# Revit family: BIM_KUBAIR F400 CC INTZ Horizontal
name_source: partatom
category: Equipement de génie climatique
revit_build: Autodesk Revit 2016 (Build: 20161004_0715(x64)
units: mm (PartAtom-declared; Revit-internal decimal feet)

## family parameters
Basée sur le plan de construction = Non
Cote de connecteur circulaire = Utiliser le diamètre
Couper avec des vides une fois chargée = Non
Numéro OmniClass = 23.75.00.00
Partagée = Non
Point de calcul de pièce = Oui
Titre OmniClass = Climate Control (HVAC)
Toujours verticalement = Oui
Type d'élément = Normal

## types (75) — shared parameters
Classe_de_protection_electrique = F
Consignes – raccordements aérauliques = Raccorder 1, 2 ou 3 ouies  au refoulement et 1, 2 ou 3 ouies à l’aspiration
Fabricant = VIM
Hauteur_equerre = 200 mm  [stored 0.656168 ft]
Hauteur_support = 30 mm  [stored 0.0984252 ft]
IfcExportAs = IfcFan
IfcExportType = IfcFlowMovingDevice
Largeur_equerre = 218 mm  [stored 0.715223 ft]
Lien_page_produit = http://www.vim.fr
Materiau_caisson = Acier, galvanisé
Materiau_support = Acier
Protection_IP = IP 55
Visibilité_marque = Oui

## per-type parameters (varying)
| type | A | BH | C | Code_article | Courant_nominal | D | Debit_maxi | Debit_mini | EC | F | J | KC | Modèle | Nombre_de_phases | Poids | Position_A_equerre | Prof_INTZ | Puissance_electrique | Tension_nominale |
| KUBAIR F400 CC 355 4PM INTZ 0,25kW Horizontal | 627 mm  [stored 2.05709 ft] | 695 mm  [stored 2.28018 ft] | 263 mm  [stored 0.862861 ft] | 644533 + 660100 | 3 A | 559 mm  [stored 1.83399 ft] | 3090 m³/h | 900 m³/h | 790 mm  [stored 2.59186 ft] | 660 mm  [stored 2.16535 ft] | 102 mm | 954 mm  [stored 3.12992 ft] | KUBAIR F400 CC 355 4PM INTZ 0,25kW Caisson Horizontal | 1 | 59 Kg | 155 mm  [stored 0.50853 ft] | 100 mm  [stored 0.328084 ft] | 250 W | 230 V |
| KUBAIR F400 CC 355 6PM INTZ 0,18kW Horizontal | 627 mm  [stored 2.05709 ft] | 695 mm  [stored 2.28018 ft] | 263 mm  [stored 0.862861 ft] | 644537 + 660100 | 2 A | 559 mm  [stored 1.83399 ft] | 2140 m³/h | 620 m³/h | 790 mm  [stored 2.59186 ft] | 660 mm  [stored 2.16535 ft] | 102 mm | 954 mm  [stored 3.12992 ft] | KUBAIR F400 CC 355 6PM INTZ 0,18kW Caisson Horizontal | 1 | 59 Kg | 155 mm  [stored 0.50853 ft] | 100 mm  [stored 0.328084 ft] | 180 W | 230 V |
| KUBAIR F400 CC 355 4PT IE1 INTZ 0,25kW Horizontal | 627 mm  [stored 2.05709 ft] | 695 mm  [stored 2.28018 ft] | 263 mm  [stored 0.862861 ft] | 644541 + 660100 | 1 A | 559 mm  [stored 1.83399 ft] | 3090 m³/h | 900 m³/h | 790 mm  [stored 2.59186 ft] | 660 mm  [stored 2.16535 ft] | 102 mm | 954 mm  [stored 3.12992 ft] | KUBAIR F400 CC 355 4PT IE1 INTZ 0,25kW Caisson Horizontal | 3 | 59 Kg | 155 mm  [stored 0.50853 ft] | 100 mm  [stored 0.328084 ft] | 250 W | 400 V |
| KUBAIR F400 CC 355 4PT IE2 INTZ 0,25kW Horizontal | 627 mm  [stored 2.05709 ft] | 695 mm  [stored 2.28018 ft] | 263 mm  [stored 0.862861 ft] | 644545 + 660100 | 1 A | 559 mm  [stored 1.83399 ft] | 3090 m³/h | 900 m³/h | 790 mm  [stored 2.59186 ft] | 660 mm  [stored 2.16535 ft] | 102 mm | 954 mm  [stored 3.12992 ft] | KUBAIR F400 CC 355 4PT IE2 INTZ 0,25kW Caisson Horizontal | 3 | 59 Kg | 155 mm  [stored 0.50853 ft] | 100 mm  [stored 0.328084 ft] | 250 W | 400 V |
| KUBAIR F400 CC 355 4PT IE3 INTZ 0,25kW Horizontal | 627 mm  [stored 2.05709 ft] | 695 mm  [stored 2.28018 ft] | 263 mm  [stored 0.862861 ft] | 644549 + 660100 | 1 A | 559 mm  [stored 1.83399 ft] | 3090 m³/h | 900 m³/h | 790 mm  [stored 2.59186 ft] | 660 mm  [stored 2.16535 ft] | 102 mm | 954 mm  [stored 3.12992 ft] | KUBAIR F400 CC 355 4PT IE3 INTZ 0,25kW Caisson Horizontal | 3 | 59 Kg | 155 mm  [stored 0.50853 ft] | 100 mm  [stored 0.328084 ft] | 250 W | 400 V |
| KUBAIR F400 CC 355 6PT IE1 INTZ 0,18kW Horizontal | 627 mm  [stored 2.05709 ft] | 695 mm  [stored 2.28018 ft] | 263 mm  [stored 0.862861 ft] | 644553 + 660100 | 1 A | 559 mm  [stored 1.83399 ft] | 2140 m³/h | 620 m³/h | 790 mm  [stored 2.59186 ft] | 660 mm  [stored 2.16535 ft] | 102 mm | 954 mm  [stored 3.12992 ft] | KUBAIR F400 CC 355 6PT IE1 INTZ 0,18kW Caisson Horizontal | 3 | 59 Kg | 155 mm  [stored 0.50853 ft] | 100 mm  [stored 0.328084 ft] | 180 W | 400 V |
| KUBAIR F400 CC 355 6PT IE2 INTZ 0,18kW Horizontal | 627 mm  [stored 2.05709 ft] | 695 mm  [stored 2.28018 ft] | 263 mm  [stored 0.862861 ft] | 644557 + 660100 | 1 A | 559 mm  [stored 1.83399 ft] | 2140 m³/h | 620 m³/h | 790 mm  [stored 2.59186 ft] | 660 mm  [stored 2.16535 ft] | 102 mm | 954 mm  [stored 3.12992 ft] | KUBAIR F400 CC 355 6PT IE2 INTZ 0,18kW Caisson Horizontal | 3 | 59 Kg | 155 mm  [stored 0.50853 ft] | 100 mm  [stored 0.328084 ft] | 180 W | 400 V |
| KUBAIR F400 CC 355 6PT IE3 INTZ 0,18kW Horizontal | 627 mm  [stored 2.05709 ft] | 695 mm  [stored 2.28018 ft] | 263 mm  [stored 0.862861 ft] | 644561 + 660100 | 1 A | 559 mm  [stored 1.83399 ft] | 2140 m³/h | 620 m³/h | 790 mm  [stored 2.59186 ft] | 660 mm  [stored 2.16535 ft] | 102 mm | 954 mm  [stored 3.12992 ft] | KUBAIR F400 CC 355 6PT IE3 INTZ 0,18kW Caisson Horizontal | 3 | 59 Kg | 155 mm  [stored 0.50853 ft] | 100 mm  [stored 0.328084 ft] | 180 W | 400 V |
| KUBAIR F400 CC 355 4/6PT INTZ 0,30/0,10kW Horizontal | 627 mm  [stored 2.05709 ft] | 695 mm  [stored 2.28018 ft] | 263 mm  [stored 0.862861 ft] | 644565 + 660100 | 1 A | 559 mm  [stored 1.83399 ft] | 3090 m³/h | 900 m³/h | 790 mm  [stored 2.59186 ft] | 660 mm  [stored 2.16535 ft] | 102 mm | 954 mm  [stored 3.12992 ft] | KUBAIR F400 CC 355 4/6PT INTZ 0,30/0,10kW Caisson Horizontal | 3 | 61 Kg | 155 mm  [stored 0.50853 ft] | 100 mm  [stored 0.328084 ft] | 300 W | 400 V |
| KUBAIR F400 CC 355 4/8PT INTZ 0,60/0,15kW Horizontal | 627 mm  [stored 2.05709 ft] | 695 mm  [stored 2.28018 ft] | 263 mm  [stored 0.862861 ft] | 644569 + 660100 | 2 A | 559 mm  [stored 1.83399 ft] | 3090 m³/h | 900 m³/h | 790 mm  [stored 2.59186 ft] | 660 mm  [stored 2.16535 ft] | 102 mm | 954 mm  [stored 3.12992 ft] | KUBAIR F400 CC 355 4/8PT INTZ 0,60/0,15kW Caisson Horizontal | 3 | 61 Kg | 155 mm  [stored 0.50853 ft] | 100 mm  [stored 0.328084 ft] | 600 W | 400 V |
| KUBAIR F400 CC 400 4PM INTZ 0,55kW Horizontal | 699 mm  [stored 2.29331 ft] | 767 mm  [stored 2.5164 ft] | 297 mm  [stored 0.974409 ft] | 644573 + 660101 | 4 A | 631 mm  [stored 2.07021 ft] | 5000 m³/h | 1060 m³/h | 864 mm  [stored 2.83465 ft] | 732 mm | 102 mm | 1022 mm | KUBAIR F400 CC 400 4PM INTZ 0,55kW Caisson Horizontal | 1 | 72 Kg | 155 mm  [stored 0.50853 ft] | 120 mm  [stored 0.393701 ft] | 550 W | 230 V |
| KUBAIR F400 CC 400 6PM INTZ 0,25kW Horizontal | 699 mm  [stored 2.29331 ft] | 767 mm  [stored 2.5164 ft] | 297 mm  [stored 0.974409 ft] | 644577 + 660101
644577 + 660101 | 2 A | 631 mm  [stored 2.07021 ft] | 3310 m³/h | 520 m³/h | 864 mm  [stored 2.83465 ft] | 732 mm | 102 mm | 1022 mm | KUBAIR F400 CC 400 6PM INTZ 0,25kW Caisson Horizontal | 1 | 72 Kg | 155 mm  [stored 0.50853 ft] | 120 mm  [stored 0.393701 ft] | 250 W | 230 V |
| KUBAIR F400 CC 400 4PT IE1 INTZ 0,55kW Horizontal | 699 mm  [stored 2.29331 ft] | 767 mm  [stored 2.5164 ft] | 297 mm  [stored 0.974409 ft] | 644581 + 660101 | 1 A | 631 mm  [stored 2.07021 ft] | 5000 m³/h | 1060 m³/h | 864 mm  [stored 2.83465 ft] | 732 mm | 102 mm | 1022 mm | KUBAIR F400 CC 400 4PT IE1 INTZ 0,55kW Caisson Horizontal | 3 | 72 Kg | 155 mm  [stored 0.50853 ft] | 120 mm  [stored 0.393701 ft] | 550 W | 400 V |
| KUBAIR F400 CC 400 4PT IE2 INTZ 0,55kW Horizontal | 699 mm  [stored 2.29331 ft] | 767 mm  [stored 2.5164 ft] | 297 mm  [stored 0.974409 ft] | 644585 + 660101 | 1 A | 631 mm  [stored 2.07021 ft] | 5000 m³/h | 1060 m³/h | 864 mm  [stored 2.83465 ft] | 732 mm | 102 mm | 1022 mm | KUBAIR F400 CC 400 4PT IE2 INTZ 0,55kW Caisson Horizontal | 3 | 72 Kg | 155 mm  [stored 0.50853 ft] | 120 mm  [stored 0.393701 ft] | 550 W | 400 V |
| KUBAIR F400 CC 400 4PT IE3 INTZ 0,55kW Horizontal | 699 mm  [stored 2.29331 ft] | 767 mm  [stored 2.5164 ft] | 297 mm  [stored 0.974409 ft] | 644589 + 660101 | 1 A | 631 mm  [stored 2.07021 ft] | 5000 m³/h | 1060 m³/h | 864 mm  [stored 2.83465 ft] | 732 mm | 102 mm | 1022 mm | KUBAIR F400 CC 400 4PT IE3 INTZ 0,55kW Caisson Horizontal | 3 | 72 Kg | 155 mm  [stored 0.50853 ft] | 120 mm  [stored 0.393701 ft] | 550 W | 400 V |
| KUBAIR F400 CC 400 6PT IE1 INTZ 0,37kW Horizontal | 699 mm  [stored 2.29331 ft] | 767 mm  [stored 2.5164 ft] | 297 mm  [stored 0.974409 ft] | 644593 + 660101 | 1 A | 631 mm  [stored 2.07021 ft] | 3310 m³/h | 520 m³/h | 864 mm  [stored 2.83465 ft] | 732 mm | 102 mm | 1022 mm | KUBAIR F400 CC 400 6PT IE1 INTZ 0,37kW Caisson Horizontal | 3 | 72 Kg | 155 mm  [stored 0.50853 ft] | 120 mm  [stored 0.393701 ft] | 370 W | 400 V |
| KUBAIR F400 CC 400 6PT IE2 INTZ 0,37kW Horizontal | 699 mm  [stored 2.29331 ft] | 767 mm  [stored 2.5164 ft] | 297 mm  [stored 0.974409 ft] | 644597 + 660101 | 1 A | 631 mm  [stored 2.07021 ft] | 3310 m³/h | 520 m³/h | 864 mm  [stored 2.83465 ft] | 732 mm | 102 mm | 1022 mm | KUBAIR F400 CC 400 6PT IE2 INTZ 0,37kW Caisson Horizontal | 3 | 72 Kg | 155 mm  [stored 0.50853 ft] | 120 mm  [stored 0.393701 ft] | 370 W | 400 V |
| KUBAIR F400 CC 400 6PT IE3 INTZ 0,37kW Horizontal | 699 mm  [stored 2.29331 ft] | 767 mm  [stored 2.5164 ft] | 297 mm  [stored 0.974409 ft] | 644601 + 660101 | 1 A | 631 mm  [stored 2.07021 ft] | 3310 m³/h | 520 m³/h | 864 mm  [stored 2.83465 ft] | 732 mm | 102 mm | 1022 mm | KUBAIR F400 CC 400 6PT IE3 INTZ 0,37kW Caisson Horizontal | 3 | 72 Kg | 155 mm  [stored 0.50853 ft] | 120 mm  [stored 0.393701 ft] | 370 W | 400 V |
| KUBAIR F400 CC 400 4/6PT INTZ 0,55/0,20kW Horizontal | 699 mm  [stored 2.29331 ft] | 767 mm  [stored 2.5164 ft] | 297 mm  [stored 0.974409 ft] | 644605 + 660101 | 2 A | 631 mm  [stored 2.07021 ft] | 5000 m³/h | 1060 m³/h | 864 mm  [stored 2.83465 ft] | 732 mm | 102 mm | 1022 mm | KUBAIR F400 CC 400 4/6PT INTZ 0,55/0,20kW Caisson Horizontal | 3 | 74 Kg | 155 mm  [stored 0.50853 ft] | 120 mm  [stored 0.393701 ft] | 550 W | 400 V |
| KUBAIR F400 CC 400 4/8PT INTZ 0,60/0,15kW Horizontal | 699 mm  [stored 2.29331 ft] | 767 mm  [stored 2.5164 ft] | 297 mm  [stored 0.974409 ft] | 644609 + 660101 | 2 A | 631 mm  [stored 2.07021 ft] | 5000 m³/h | 1060 m³/h | 864 mm  [stored 2.83465 ft] | 732 mm | 102 mm | 1022 mm | KUBAIR F400 CC 400 4/8PT INTZ 0,60/0,15kW Caisson Horizontal | 3 | 74 Kg | 155 mm  [stored 0.50853 ft] | 120 mm  [stored 0.393701 ft] | 600 W | 400 V |
| KUBAIR F400 CC 450 6PM INTZ 0,25kW Horizontal | 779 mm  [stored 2.55577 ft] | 847 mm | 326 mm  [stored 1.06955 ft] | 644613 + 660102 | 2 A | 711 mm  [stored 2.33268 ft] | 4750 m³/h | 820 m³/h | 990 mm | 812 mm  [stored 2.66404 ft] | 102 mm | 1081 mm | KUBAIR F400 CC 450 6PM INTZ 0,25kW Caisson Horizontal | 1 | 92 Kg | 175 mm | 120 mm  [stored 0.393701 ft] | 250 W | 230 V |
| KUBAIR F400 CC 450 4PT IE2 INTZ 1,1kW Horizontal | 779 mm  [stored 2.55577 ft] | 847 mm | 326 mm  [stored 1.06955 ft] | 644617 + 660102 | 2 A | 711 mm  [stored 2.33268 ft] | 7080 m³/h | 1230 m³/h | 990 mm | 812 mm  [stored 2.66404 ft] | 102 mm | 1081 mm | KUBAIR F400 CC 450 4PT IE2 INTZ 1,1kW Caisson Horizontal | 3 | 92 Kg | 175 mm | 120 mm  [stored 0.393701 ft] | 1100 W | 400 V |
| KUBAIR F400 CC 450 4PT IE3 INTZ 1,1kW Horizontal | 779 mm  [stored 2.55577 ft] | 847 mm | 326 mm  [stored 1.06955 ft] | 644621 + 660102 | 2 A | 711 mm  [stored 2.33268 ft] | 7080 m³/h | 1230 m³/h | 990 mm | 812 mm  [stored 2.66404 ft] | 102 mm | 1081 mm | KUBAIR F400 CC 450 4PT IE3 INTZ 1,1kW Caisson Horizontal | 3 | 92 Kg | 175 mm | 120 mm  [stored 0.393701 ft] | 1100 W | 400 V |
| KUBAIR F400 CC 450 6PT IE1 INTZ 0,37kW Horizontal | 779 mm  [stored 2.55577 ft] | 847 mm | 326 mm  [stored 1.06955 ft] | 644625 + 660102 | 1 A | 711 mm  [stored 2.33268 ft] | 4750 m³/h | 820 m³/h | 990 mm | 812 mm  [stored 2.66404 ft] | 102 mm | 1081 mm | KUBAIR F400 CC 450 6PT IE1 INTZ 0,37kW Caisson Horizontal | 3 | 92 Kg | 175 mm | 120 mm  [stored 0.393701 ft] | 370 W | 400 V |
| KUBAIR F400 CC 450 6PT IE2 INTZ 0,37kW Horizontal | 779 mm  [stored 2.55577 ft] | 847 mm | 326 mm  [stored 1.06955 ft] | 644629 + 660102 | 1 A | 711 mm  [stored 2.33268 ft] | 4750 m³/h | 820 m³/h | 990 mm | 812 mm  [stored 2.66404 ft] | 102 mm | 1081 mm | KUBAIR F400 CC 450 6PT IE2 INTZ 0,37kW Caisson Horizontal | 3 | 92 Kg | 175 mm | 120 mm  [stored 0.393701 ft] | 370 W | 400 V |
| KUBAIR F400 CC 450 6PT IE3 INTZ 0,37kW Horizontal | 779 mm  [stored 2.55577 ft] | 847 mm | 326 mm  [stored 1.06955 ft] | 644633 + 660102 | 1 A | 711 mm  [stored 2.33268 ft] | 4750 m³/h | 820 m³/h | 990 mm | 812 mm  [stored 2.66404 ft] | 102 mm | 1081 mm | KUBAIR F400 CC 450 6PT IE3 INTZ 0,37kW Caisson Horizontal | 3 | 92 Kg | 175 mm | 120 mm  [stored 0.393701 ft] | 370 W | 400 V |
| KUBAIR F400 CC 450 8PT IE1 INTZ 0,18kW Horizontal | 779 mm  [stored 2.55577 ft] | 847 mm | 326 mm  [stored 1.06955 ft] | 644637 + 660102 | 1 A | 711 mm  [stored 2.33268 ft] | 3420 m³/h | 590 m³/h | 990 mm | 812 mm  [stored 2.66404 ft] | 102 mm | 1081 mm | KUBAIR F400 CC 450 8PT IE1 INTZ 0,18kW Caisson Horizontal | 3 | 92 Kg | 175 mm | 120 mm  [stored 0.393701 ft] | 180 W | 400 V |
| KUBAIR F400 CC 450 8PT IE2 INTZ 0,18kW Horizontal | 779 mm  [stored 2.55577 ft] | 847 mm | 326 mm  [stored 1.06955 ft] | 644641 + 660102 | 1 A | 711 mm  [stored 2.33268 ft] | 3420 m³/h | 590 m³/h | 990 mm | 812 mm  [stored 2.66404 ft] | 102 mm | 1081 mm | KUBAIR F400 CC 450 8PT IE2 INTZ 0,18kW Caisson Horizontal | 3 | 92 Kg | 175 mm | 120 mm  [stored 0.393701 ft] | 180 W | 400 V |
| KUBAIR F400 CC 450 8PT IE3 INTZ 0,18kW Horizontal | 779 mm  [stored 2.55577 ft] | 847 mm | 326 mm  [stored 1.06955 ft] | 644645 + 660102 | 1 A | 711 mm  [stored 2.33268 ft] | 3420 m³/h | 590 m³/h | 990 mm | 812 mm  [stored 2.66404 ft] | 102 mm | 1081 mm | KUBAIR F400 CC 450 8PT IE3 INTZ 0,18kW Caisson Horizontal | 3 | 92 Kg | 175 mm | 120 mm  [stored 0.393701 ft] | 180 W | 400 V |
| KUBAIR F400 CC 450 4/6PT INTZ 1,10/0,30kW Horizontal | 779 mm  [stored 2.55577 ft] | 847 mm | 326 mm  [stored 1.06955 ft] | 644649 + 660102 | 3 A | 711 mm  [stored 2.33268 ft] | 7080 m³/h | 1230 m³/h | 990 mm | 812 mm  [stored 2.66404 ft] | 102 mm | 1081 mm | KUBAIR F400 CC 450 4/6PT INTZ 1,10/0,30kW Caisson Horizontal | 3 | 94 Kg | 175 mm | 120 mm  [stored 0.393701 ft] | 1100 W | 400 V |
| KUBAIR F400 CC 450 4/8PT INTZ 1,20/0,30kW Horizontal | 779 mm  [stored 2.55577 ft] | 847 mm | 326 mm  [stored 1.06955 ft] | 644653 + 660102 | 3 A | 711 mm  [stored 2.33268 ft] | 7080 m³/h | 1230 m³/h | 990 mm | 812 mm  [stored 2.66404 ft] | 102 mm | 1081 mm | KUBAIR F400 CC 450 4/8PT INTZ 1,20/0,30kW Caisson Horizontal | 3 | 94 Kg | 175 mm | 120 mm  [stored 0.393701 ft] | 1200 W | 400 V |
| KUBAIR F400 CC 450 6/8PT INTZ 0,37/0,20kW Horizontal | 779 mm  [stored 2.55577 ft] | 847 mm | 326 mm  [stored 1.06955 ft] | 644657 + 660102 | 1 A | 711 mm  [stored 2.33268 ft] | 4750 m³/h | 820 m³/h | 990 mm | 812 mm  [stored 2.66404 ft] | 102 mm | 1081 mm | KUBAIR F400 CC 450 6/8PT INTZ 0,37/0,20kW Caisson Horizontal | 3 | 94 Kg | 175 mm | 120 mm  [stored 0.393701 ft] | 370 W | 400 V |
| KUBAIR F400 CC 500 6PM INTZ 0,37kW Horizontal | 858 mm | 925 mm | 338 mm  [stored 1.10892 ft] | 644661 + 660103 | 3 A | 768 mm  [stored 2.51969 ft] | 5960 m³/h | 920 m³/h | 1039 mm | 890 mm | 112 mm  [stored 0.367454 ft] | 1145 mm | KUBAIR F400 CC 500 6PM INTZ 0,37kW Caisson Horizontal | 1 | 114 Kg | 175 mm | 120 mm  [stored 0.393701 ft] | 370 W | 230 V |
| KUBAIR F400 CC 500 4PT IE2 INTZ 1,5kW Horizontal | 858 mm | 925 mm | 338 mm  [stored 1.10892 ft] | 644665 + 660103 | 3 A | 768 mm  [stored 2.51969 ft] | 8850 m³/h | 1370 m³/h | 1039 mm | 890 mm | 112 mm  [stored 0.367454 ft] | 1145 mm | KUBAIR F400 CC 500 4PT IE2 INTZ 1,5kW Caisson Horizontal | 3 | 114 Kg | 175 mm | 120 mm  [stored 0.393701 ft] | 1500 W | 400 V |
| KUBAIR F400 CC 500 4PT IE3 INTZ 1,5kW Horizontal | 858 mm | 925 mm | 338 mm  [stored 1.10892 ft] | 644669 + 660103 | 3 A | 768 mm  [stored 2.51969 ft] | 8850 m³/h | 1370 m³/h | 1039 mm | 890 mm | 112 mm  [stored 0.367454 ft] | 1145 mm | KUBAIR F400 CC 500 4PT IE3 INTZ 1,5kW Caisson Horizontal | 3 | 114 Kg | 175 mm | 120 mm  [stored 0.393701 ft] | 1500 W | 400 V |
| KUBAIR F400 CC 500 6PT IE1 INTZ 0,55kW Horizontal | 858 mm | 925 mm | 338 mm  [stored 1.10892 ft] | 644673 + 660103 | 2 A | 768 mm  [stored 2.51969 ft] | 5960 m³/h | 920 m³/h | 1039 mm | 890 mm | 112 mm  [stored 0.367454 ft] | 1145 mm | KUBAIR F400 CC 500 6PT IE1 INTZ 0,55kW Caisson Horizontal | 3 | 114 Kg | 175 mm | 120 mm  [stored 0.393701 ft] | 550 W | 400 V |
| KUBAIR F400 CC 500 6PT IE2 INTZ 0,55kW Horizontal | 858 mm | 925 mm | 338 mm  [stored 1.10892 ft] | 644677 + 660103 | 1 A | 768 mm  [stored 2.51969 ft] | 5960 m³/h | 920 m³/h | 1039 mm | 890 mm | 112 mm  [stored 0.367454 ft] | 1145 mm | KUBAIR F400 CC 500 6PT IE2 INTZ 0,55kW Caisson Horizontal | 3 | 114 Kg | 175 mm | 120 mm  [stored 0.393701 ft] | 550 W | 400 V |
| KUBAIR F400 CC 500 6PT IE3 INTZ 0,55kW Horizontal | 858 mm | 925 mm | 338 mm  [stored 1.10892 ft] | 644681 + 660103 | 1 A | 768 mm  [stored 2.51969 ft] | 5960 m³/h | 920 m³/h | 1039 mm | 890 mm | 112 mm  [stored 0.367454 ft] | 1145 mm | KUBAIR F400 CC 500 6PT IE3 INTZ 0,55kW Caisson Horizontal | 3 | 114 Kg | 175 mm | 120 mm  [stored 0.393701 ft] | 550 W | 400 V |
| KUBAIR F400 CC 500 8PT IE1 INTZ 0,18kW Horizontal | 858 mm | 925 mm | 338 mm  [stored 1.10892 ft] | 644685 + 660103 | 1 A | 768 mm  [stored 2.51969 ft] | 4280 m³/h | 660 m³/h | 1039 mm | 890 mm | 112 mm  [stored 0.367454 ft] | 1145 mm | KUBAIR F400 CC 500 8PT IE1 INTZ 0,18kW Caisson Horizontal | 3 | 114 Kg | 175 mm | 120 mm  [stored 0.393701 ft] | 180 W | 400 V |
| KUBAIR F400 CC 500 8PT IE2 INTZ 0,18kW Horizontal | 858 mm | 925 mm | 338 mm  [stored 1.10892 ft] | 644689 + 660103 | 1 A | 768 mm  [stored 2.51969 ft] | 4280 m³/h | 660 m³/h | 1039 mm | 890 mm | 112 mm  [stored 0.367454 ft] | 1145 mm | KUBAIR F400 CC 500 8PT IE2 INTZ 0,18kW Caisson Horizontal | 3 | 114 Kg | 175 mm | 120 mm  [stored 0.393701 ft] | 180 W | 400 V |
| KUBAIR F400 CC 500 8PT IE3 INTZ 0,18kW Horizontal | 858 mm | 925 mm | 338 mm  [stored 1.10892 ft] | 644693 + 660103 | 1 A | 768 mm  [stored 2.51969 ft] | 4280 m³/h | 660 m³/h | 1039 mm | 890 mm | 112 mm  [stored 0.367454 ft] | 1145 mm | KUBAIR F400 CC 500 8PT IE3 INTZ 0,18kW Caisson Horizontal | 3 | 114 Kg | 175 mm | 120 mm  [stored 0.393701 ft] | 180 W | 400 V |
| KUBAIR F400 CC 500 4/6PT INTZ 1,50/0,37kW Horizontal | 858 mm | 925 mm | 338 mm  [stored 1.10892 ft] | 644697 + 660103 | 4 A | 768 mm  [stored 2.51969 ft] | 8850 m³/h | 1370 m³/h | 1039 mm | 890 mm | 112 mm  [stored 0.367454 ft] | 1145 mm | KUBAIR F400 CC 500 4/6PT INTZ 1,50/0,37kW Caisson Horizontal | 3 | 116 Kg | 175 mm | 120 mm  [stored 0.393701 ft] | 1500 W | 400 V |
| KUBAIR F400 CC 500 4/8PT INTZ 1,60/0,40kW Horizontal | 858 mm | 925 mm | 338 mm  [stored 1.10892 ft] | 644701 + 660103 | 4 A | 768 mm  [stored 2.51969 ft] | 8850 m³/h | 1370 m³/h | 1039 mm | 890 mm | 112 mm  [stored 0.367454 ft] | 1145 mm | KUBAIR F400 CC 500 4/8PT INTZ 1,60/0,40kW Caisson Horizontal | 3 | 116 Kg | 175 mm | 120 mm  [stored 0.393701 ft] | 1600 W | 400 V |
| KUBAIR F400 CC 500 6/8PT INTZ 0,55/0,37kW Horizontal | 858 mm | 925 mm | 338 mm  [stored 1.10892 ft] | 644705 + 660103 | 2 A | 768 mm  [stored 2.51969 ft] | 5960 m³/h | 920 m³/h | 1039 mm | 890 mm | 112 mm  [stored 0.367454 ft] | 1145 mm | KUBAIR F400 CC 500 6/8PT INTZ 0,55/0,37kW Caisson Horizontal | 3 | 116 Kg | 175 mm | 120 mm  [stored 0.393701 ft] | 550 W | 400 V |
| KUBAIR F400 CC 560 4PT IE2 INTZ 2,2kW Horizontal | 954 mm  [stored 3.12992 ft] | 1021 mm | 354 mm | 644709 + 660104 | 5 A | 864 mm  [stored 2.83465 ft] | 11330 m³/h | 1520 m³/h | 1139 mm | 986 mm | 112 mm  [stored 0.367454 ft] | 1178 mm | KUBAIR F400 CC 560 4PT IE2 INTZ 2,2kW Caisson Horizontal | 3 | 159 Kg | 213 mm | 120 mm  [stored 0.393701 ft] | 2200 W | 400 V |
| KUBAIR F400 CC 560 4PT IE3 INTZ 2,2kW Horizontal | 954 mm  [stored 3.12992 ft] | 1021 mm | 354 mm | 644713 + 660104 | 5 A | 864 mm  [stored 2.83465 ft] | 11330 m³/h | 1520 m³/h | 1139 mm | 986 mm | 112 mm  [stored 0.367454 ft] | 1178 mm | KUBAIR F400 CC 560 4PT IE3 INTZ 2,2kW Caisson Horizontal | 3 | 159 Kg | 213 mm | 120 mm  [stored 0.393701 ft] | 2200 W | 400 V |
| KUBAIR F400 CC 560 6PT IE2 INTZ 0,75kW Horizontal | 954 mm  [stored 3.12992 ft] | 1021 mm | 354 mm | 644717 + 660104 | 2 A | 864 mm  [stored 2.83465 ft] | 7630 m³/h | 1020 m³/h | 1139 mm | 986 mm | 112 mm  [stored 0.367454 ft] | 1178 mm | KUBAIR F400 CC 560 6PT IE2 INTZ 0,75kW Caisson Horizontal | 3 | 159 Kg | 213 mm | 120 mm  [stored 0.393701 ft] | 750 W | 400 V |
| KUBAIR F400 CC 560 6PT IE3 INTZ 0,75kW Horizontal | 954 mm  [stored 3.12992 ft] | 1021 mm | 354 mm | 644721 + 660104 | 2 A | 864 mm  [stored 2.83465 ft] | 7630 m³/h | 1020 m³/h | 1139 mm | 986 mm | 112 mm  [stored 0.367454 ft] | 1178 mm | KUBAIR F400 CC 560 6PT IE3 INTZ 0,75kW Caisson Horizontal | 3 | 159 Kg | 213 mm | 120 mm  [stored 0.393701 ft] | 750 W | 400 V |
| KUBAIR F400 CC 560 8PT IE1 INTZ 0,37kW Horizontal | 954 mm  [stored 3.12992 ft] | 1021 mm | 354 mm | 644725 + 660104 | 1 A | 864 mm  [stored 2.83465 ft] | 5490 m³/h | 740 m³/h | 1139 mm | 986 mm | 112 mm  [stored 0.367454 ft] | 1178 mm | KUBAIR F400 CC 560 8PT IE1 INTZ 0,37kW Caisson Horizontal | 3 | 159 Kg | 213 mm | 120 mm  [stored 0.393701 ft] | 370 W | 400 V |
| KUBAIR F400 CC 560 8PT IE2 INTZ 0,37kW Horizontal | 954 mm  [stored 3.12992 ft] | 1021 mm | 354 mm | 644729 + 660104 | 1 A | 864 mm  [stored 2.83465 ft] | 5490 m³/h | 740 m³/h | 1139 mm | 986 mm | 112 mm  [stored 0.367454 ft] | 1178 mm | KUBAIR F400 CC 560 8PT IE2 INTZ 0,37kW Caisson Horizontal | 3 | 159 Kg | 213 mm | 120 mm  [stored 0.393701 ft] | 370 W | 400 V |
| KUBAIR F400 CC 560 8PT IE3 INTZ 0,37kW Horizontal | 954 mm  [stored 3.12992 ft] | 1021 mm | 354 mm | 644733 + 660104 | 1 A | 864 mm  [stored 2.83465 ft] | 5490 m³/h | 740 m³/h | 1139 mm | 986 mm | 112 mm  [stored 0.367454 ft] | 1178 mm | KUBAIR F400 CC 560 8PT IE3 INTZ 0,37kW Caisson Horizontal | 3 | 159 Kg | 213 mm | 120 mm  [stored 0.393701 ft] | 370 W | 400 V |
| KUBAIR F400 CC 560 4/6PT INTZ 2,20/0,70kW Horizontal | 954 mm  [stored 3.12992 ft] | 1021 mm | 354 mm | 644737 + 660104 | 5 A | 864 mm  [stored 2.83465 ft] | 11330 m³/h | 1520 m³/h | 1139 mm | 986 mm | 112 mm  [stored 0.367454 ft] | 1178 mm | KUBAIR F400 CC 560 4/6PT INTZ 2,20/0,70kW Caisson Horizontal | 3 | 161 Kg | 213 mm | 120 mm  [stored 0.393701 ft] | 2200 W | 400 V |
| KUBAIR F400 CC 560 4/8PT INTZ 2,20/0,55kW Horizontal | 954 mm  [stored 3.12992 ft] | 1021 mm | 354 mm | 644741 + 660104 | 5 A | 864 mm  [stored 2.83465 ft] | 11330 m³/h | 1520 m³/h | 1139 mm | 986 mm | 112 mm  [stored 0.367454 ft] | 1178 mm | KUBAIR F400 CC 560 4/8PT INTZ 2,20/0,55kW Caisson Horizontal | 3 | 161 Kg | 213 mm | 120 mm  [stored 0.393701 ft] | 2200 W | 400 V |
| KUBAIR F400 CC 560 6/8PT INTZ 0,75/0,37kW Horizontal | 954 mm  [stored 3.12992 ft] | 1021 mm | 354 mm | 644745 + 660104 | 2 A | 864 mm  [stored 2.83465 ft] | 7630 m³/h | 1020 m³/h | 1139 mm | 986 mm | 112 mm  [stored 0.367454 ft] | 1178 mm | KUBAIR F400 CC 560 6/8PT INTZ 0,75/0,37kW Caisson Horizontal | 3 | 161 Kg | 213 mm | 120 mm  [stored 0.393701 ft] | 750 W | 400 V |
| KUBAIR F400 CC 630 6PT IE2 INTZ 1,1kW Horizontal | 1066 mm | 1133 mm | 403 mm  [stored 1.32218 ft] | 644749 + 660105 | 3 A | 977 mm | 10000 m³/h | 1150 m³/h | 1183 mm | 1098 mm | 112 mm  [stored 0.367454 ft] | 1273 mm | KUBAIR F400 CC 630 6PT IE2 INTZ 1,1kW Caisson Horizontal | 3 | 162 Kg | 213 mm | 120 mm  [stored 0.393701 ft] | 1100 W | 400 V |
| KUBAIR F400 CC 630 6PT IE3 INTZ 1,1kW Horizontal | 1066 mm | 1133 mm | 403 mm  [stored 1.32218 ft] | 644753 + 660105 | 3 A | 977 mm | 10000 m³/h | 1150 m³/h | 1183 mm | 1098 mm | 112 mm  [stored 0.367454 ft] | 1273 mm | KUBAIR F400 CC 630 6PT IE3 INTZ 1,1kW Caisson Horizontal | 3 | 162 Kg | 213 mm | 120 mm  [stored 0.393701 ft] | 1100 W | 400 V |
| KUBAIR F400 CC 630 8PT IE1 INTZ 0,55kW Horizontal | 1066 mm | 1133 mm | 403 mm  [stored 1.32218 ft] | 644757 + 660105 | 2 A | 977 mm | 7270 m³/h | 860 m³/h | 1183 mm | 1098 mm | 112 mm  [stored 0.367454 ft] | 1273 mm | KUBAIR F400 CC 630 8PT IE1 INTZ 0,55kW Caisson Horizontal | 3 | 163 Kg | 213 mm | 120 mm  [stored 0.393701 ft] | 550 W | 400 V |
| KUBAIR F400 CC 630 8PT IE2 INTZ 0,55kW Horizontal | 1066 mm | 1133 mm | 403 mm  [stored 1.32218 ft] | 644761 + 660105 | 2 A | 977 mm | 7270 m³/h | 860 m³/h | 1183 mm | 1098 mm | 112 mm  [stored 0.367454 ft] | 1273 mm | KUBAIR F400 CC 630 8PT IE2 INTZ 0,55kW Caisson Horizontal | 3 | 163 Kg | 213 mm | 120 mm  [stored 0.393701 ft] | 550 W | 400 V |
| KUBAIR F400 CC 630 8PT IE3 INTZ 0,55kW Horizontal | 1066 mm | 1133 mm | 403 mm  [stored 1.32218 ft] | 644765 + 660105 | 2 A | 977 mm | 7270 m³/h | 860 m³/h | 1183 mm | 1098 mm | 112 mm  [stored 0.367454 ft] | 1273 mm | KUBAIR F400 CC 630 8PT IE3 INTZ 0,55kW Caisson Horizontal | 3 | 163 Kg | 213 mm | 120 mm  [stored 0.393701 ft] | 550 W | 400 V |
| KUBAIR F400 CC 630 6/8PT INTZ 1,10/0,55kW Horizontal | 1066 mm | 1133 mm | 403 mm  [stored 1.32218 ft] | 644769 + 660105 | 4 A | 977 mm | 10000 m³/h | 1150 m³/h | 1183 mm | 1098 mm | 112 mm  [stored 0.367454 ft] | 1273 mm | KUBAIR F400 CC 630 6/8PT INTZ 1,10/0,55kW Caisson Horizontal | 3 | 164 Kg | 213 mm | 120 mm  [stored 0.393701 ft] | 1100 W | 400 V |
| KUBAIR F400 CC 630 6/12PT INTZ 1,10/0,22kW Horizontal | 1066 mm | 1133 mm | 403 mm  [stored 1.32218 ft] | 644773 + 660105 | 4 A | 977 mm | 10000 m³/h | 1150 m³/h | 1183 mm | 1098 mm | 112 mm  [stored 0.367454 ft] | 1273 mm | KUBAIR F400 CC 630 6/12PT INTZ 1,10/0,22kW Caisson Horizontal | 3 | 164 Kg | 213 mm | 120 mm  [stored 0.393701 ft] | 1100 W | 400 V |
| KUBAIR F400 CC 710 6PT IE2 INTZ 3,0kW Horizontal | 1194 mm | 1261 mm | 462 mm  [stored 1.51575 ft] | 644777 + 660106 | 7 A | 1104 mm | 18900 m³/h | 420 m³/h | 1325 mm | 1226 mm | 112 mm  [stored 0.367454 ft] | 1488 mm | KUBAIR F400 CC 710 6PT IE2 INTZ 3,0kW Caisson Horizontal | 3 | 264 Kg | 234 mm  [stored 0.767717 ft] | 120 mm  [stored 0.393701 ft] | 3000 W | 400 V |
| KUBAIR F400 CC 710 6PT IE3 INTZ 3,0kW Horizontal | 1194 mm | 1261 mm | 462 mm  [stored 1.51575 ft] | 644781 + 660106 | 7 A | 1104 mm | 18900 m³/h | 420 m³/h | 1325 mm | 1226 mm | 112 mm  [stored 0.367454 ft] | 1488 mm | KUBAIR F400 CC 710 6PT IE3 INTZ 3,0kW Caisson Horizontal | 3 | 264 Kg | 234 mm  [stored 0.767717 ft] | 120 mm  [stored 0.393701 ft] | 3000 W | 400 V |
| KUBAIR F400 CC 710 8PT IE1 INTZ 2,2kW Horizontal | 1194 mm | 1261 mm | 462 mm  [stored 1.51575 ft] | 644785 + 660106 | 5 A | 1104 mm | 13600 m³/h | 300 m³/h | 1325 mm | 1226 mm | 112 mm  [stored 0.367454 ft] | 1488 mm | KUBAIR F400 CC 710 8PT IE1 INTZ 2,2kW Caisson Horizontal | 3 | 265 Kg | 234 mm  [stored 0.767717 ft] | 120 mm  [stored 0.393701 ft] | 2200 W | 400 V |
| KUBAIR F400 CC 710 8PT IE2 INTZ 2,2kW Horizontal | 1194 mm | 1261 mm | 462 mm  [stored 1.51575 ft] | 644789 + 660106 | 5 A | 1104 mm | 13600 m³/h | 300 m³/h | 1325 mm | 1226 mm | 112 mm  [stored 0.367454 ft] | 1488 mm | KUBAIR F400 CC 710 8PT IE2 INTZ 2,2kW Caisson Horizontal | 3 | 265 Kg | 234 mm  [stored 0.767717 ft] | 120 mm  [stored 0.393701 ft] | 2200 W | 400 V |
| KUBAIR F400 CC 710 8PT IE3 INTZ 2,2kW Horizontal | 1194 mm | 1261 mm | 462 mm  [stored 1.51575 ft] | 644793 + 660106 | 5 A | 1104 mm | 13600 m³/h | 300 m³/h | 1325 mm | 1226 mm | 112 mm  [stored 0.367454 ft] | 1488 mm | KUBAIR F400 CC 710 8PT IE3 INTZ 2,2kW Caisson Horizontal | 3 | 265 Kg | 234 mm  [stored 0.767717 ft] | 120 mm  [stored 0.393701 ft] | 2200 W | 400 V |
| KUBAIR F400 CC 710 6/8PT INTZ 3,00/0,75kW Horizontal | 1194 mm | 1261 mm | 462 mm  [stored 1.51575 ft] | 644797 + 660106 | 8 A | 1104 mm | 18900 m³/h | 420 m³/h | 1325 mm | 1226 mm | 112 mm  [stored 0.367454 ft] | 1488 mm | KUBAIR F400 CC 710 6/8PT INTZ 3,00/0,75kW Caisson Horizontal | 3 | 266 Kg | 234 mm  [stored 0.767717 ft] | 120 mm  [stored 0.393701 ft] | 3000 W | 400 V |
| KUBAIR F400 CC 710 6/12PT INTZ 4,0/1,0kW Horizontal | 1194 mm | 1261 mm | 462 mm  [stored 1.51575 ft] | 644801 + 660106 | 13 A | 1104 mm | 18900 m³/h | 420 m³/h | 1325 mm | 1226 mm | 112 mm  [stored 0.367454 ft] | 1488 mm | KUBAIR F400 CC 710 6/12PT INTZ 4,0/1,0kW Caisson Horizontal | 3 | 266 Kg | 234 mm  [stored 0.767717 ft] | 120 mm  [stored 0.393701 ft] | 4000 W | 400 V |
| KUBAIR F400 CC 800 6PT IE2 INTZ 4,0kW Horizontal | 1338 mm | 1420 mm | 488 mm  [stored 1.60105 ft] | 644805 + 660107 | 9 A | 1248 mm | 23390 m³/h | 660 m³/h | 1379 mm | 1370 mm | 127 mm  [stored 0.416667 ft] | 1540 mm | KUBAIR F400 CC 800 6PT IE2 INTZ 4,0kW Caisson Horizontal | 3 | 307 Kg | 234 mm  [stored 0.767717 ft] | 120 mm  [stored 0.393701 ft] | 4000 W | 400 V |
| KUBAIR F400 CC 800 6PT IE3 INTZ 4,0kW Horizontal | 1338 mm | 1420 mm | 488 mm  [stored 1.60105 ft] | 644809 + 660107 | 9 A | 1248 mm | 23390 m³/h | 660 m³/h | 1379 mm | 1370 mm | 127 mm  [stored 0.416667 ft] | 1540 mm | KUBAIR F400 CC 800 6PT IE3 INTZ 4,0kW Caisson Horizontal | 3 | 307 Kg | 234 mm  [stored 0.767717 ft] | 120 mm  [stored 0.393701 ft] | 4000 W | 400 V |
| KUBAIR F400 CC 800 8PT IE1 INTZ 2,2kW Horizontal | 1338 mm | 1420 mm | 488 mm  [stored 1.60105 ft] | 644813 + 660107 | 5 A | 1248 mm | 16910 m³/h | 480 m³/h | 1379 mm | 1370 mm | 127 mm  [stored 0.416667 ft] | 1540 mm | KUBAIR F400 CC 800 8PT IE1 INTZ 2,2kW Caisson Horizontal | 3 | 308 Kg | 234 mm  [stored 0.767717 ft] | 120 mm  [stored 0.393701 ft] | 2200 W | 400 V |
| KUBAIR F400 CC 800 8PT IE2 INTZ 2,2kW Horizontal | 1338 mm | 1420 mm | 488 mm  [stored 1.60105 ft] | 644817 + 660107 | 5 A | 1248 mm | 16910 m³/h | 480 m³/h | 1379 mm | 1370 mm | 127 mm  [stored 0.416667 ft] | 1540 mm | KUBAIR F400 CC 800 8PT IE2 INTZ 2,2kW Caisson Horizontal | 3 | 308 Kg | 234 mm  [stored 0.767717 ft] | 120 mm  [stored 0.393701 ft] | 2200 W | 400 V |
| KUBAIR F400 CC 800 8PT IE3 INTZ 2,2kW Horizontal | 1338 mm | 1420 mm | 488 mm  [stored 1.60105 ft] | 644821 + 660107 | 5 A | 1248 mm | 16910 m³/h | 480 m³/h | 1379 mm | 1370 mm | 127 mm  [stored 0.416667 ft] | 1540 mm | KUBAIR F400 CC 800 8PT IE3 INTZ 2,2kW Caisson Horizontal | 3 | 308 Kg | 234 mm  [stored 0.767717 ft] | 120 mm  [stored 0.393701 ft] | 2200 W | 400 V |
| KUBAIR F400 CC 800 6/8PT INTZ 4,0/1,1kW Horizontal | 1338 mm | 1420 mm | 488 mm  [stored 1.60105 ft] | 644825 + 660107 | 16 A | 1248 mm | 23390 m³/h | 660 m³/h | 1379 mm | 1370 mm | 127 mm  [stored 0.416667 ft] | 1540 mm | KUBAIR F400 CC 800 6/8PT INTZ 4,0/1,1kW Caisson Horizontal | 3 | 309 Kg | 234 mm  [stored 0.767717 ft] | 120 mm  [stored 0.393701 ft] | 4000 W | 400 V |
| KUBAIR F400 CC 800 6/12PT INTZ 4,0/1,0kW Horizontal | 1338 mm | 1420 mm | 488 mm  [stored 1.60105 ft] | 644829 + 660107 | 13 A | 1248 mm | 23390 m³/h | 660 m³/h | 1379 mm | 1370 mm | 127 mm  [stored 0.416667 ft] | 1540 mm | KUBAIR F400 CC 800 6/12PT INTZ 4,0/1,0kW Caisson Horizontal | 3 | 309 Kg | 234 mm  [stored 0.767717 ft] | 120 mm  [stored 0.393701 ft] | 4000 W | 400 V |

note: [stored X ft] marks values corroborated as IEEE doubles in the binary element streams (Revit-internal decimal feet)

## geometry (parser evidence)
native form markers: Blend x12
no freeform markers — native parametric forms only
